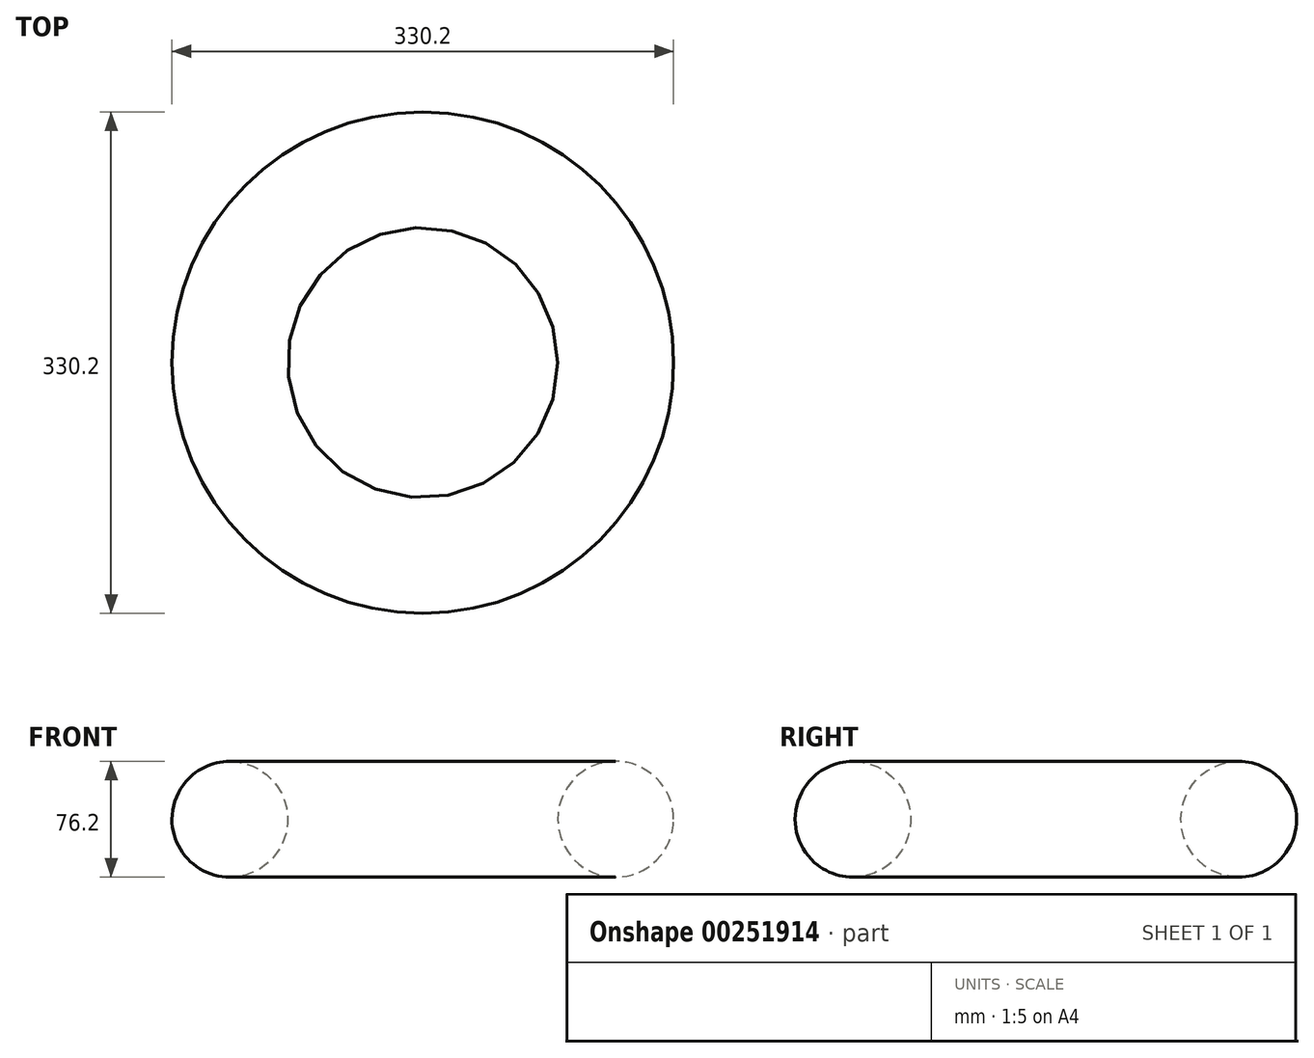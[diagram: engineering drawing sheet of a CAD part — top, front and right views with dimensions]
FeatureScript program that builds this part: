
annotation { "Feature Type Name" : "Feature", "Feature Type Description" : "" }
export const myFeature = defineFeature(function(context is Context, id is Id, definition is map)
    precondition{}
    {
        {
            var Q0;
            Q0=qCreatedBy(makeId("Front.planeOp"),FACE);
            var sketch = newSketch(context, id + "F0", { "sketchPlane" : qUnion([Q0])});
            skCircle(sketch, "E0", {"center": v(-127, 37.42) * mm, "radius": 38.1 * mm});
            skLineSegment(sketch, "E1", {"start": v(0, 75.15) * mm, "end": v(0, -76.1) * mm, "construction": true});
            skSolve(sketch);
        }
        {
            var Q0;
            Q0=makeQuery(id+"F0.imprint","IMPRINT",FACE,{"disambiguationData":[TD([[makeQuery(id+"F0.imprint","IMPRINT",EDGE,{"derivedFrom":sQuery(id+"F0.wireOp",EDGE,"E0")}),1.0]])]});
            var Q1;
            Q1=sQuery(id+"F0.wireOp",EDGE,"E1");
            revolve(context, id + "F1", {"entities" : qUnion([Q0]), "axis" : qUnion([Q1]), "revolveType" : RevolveType.FULL});
        }
    });
